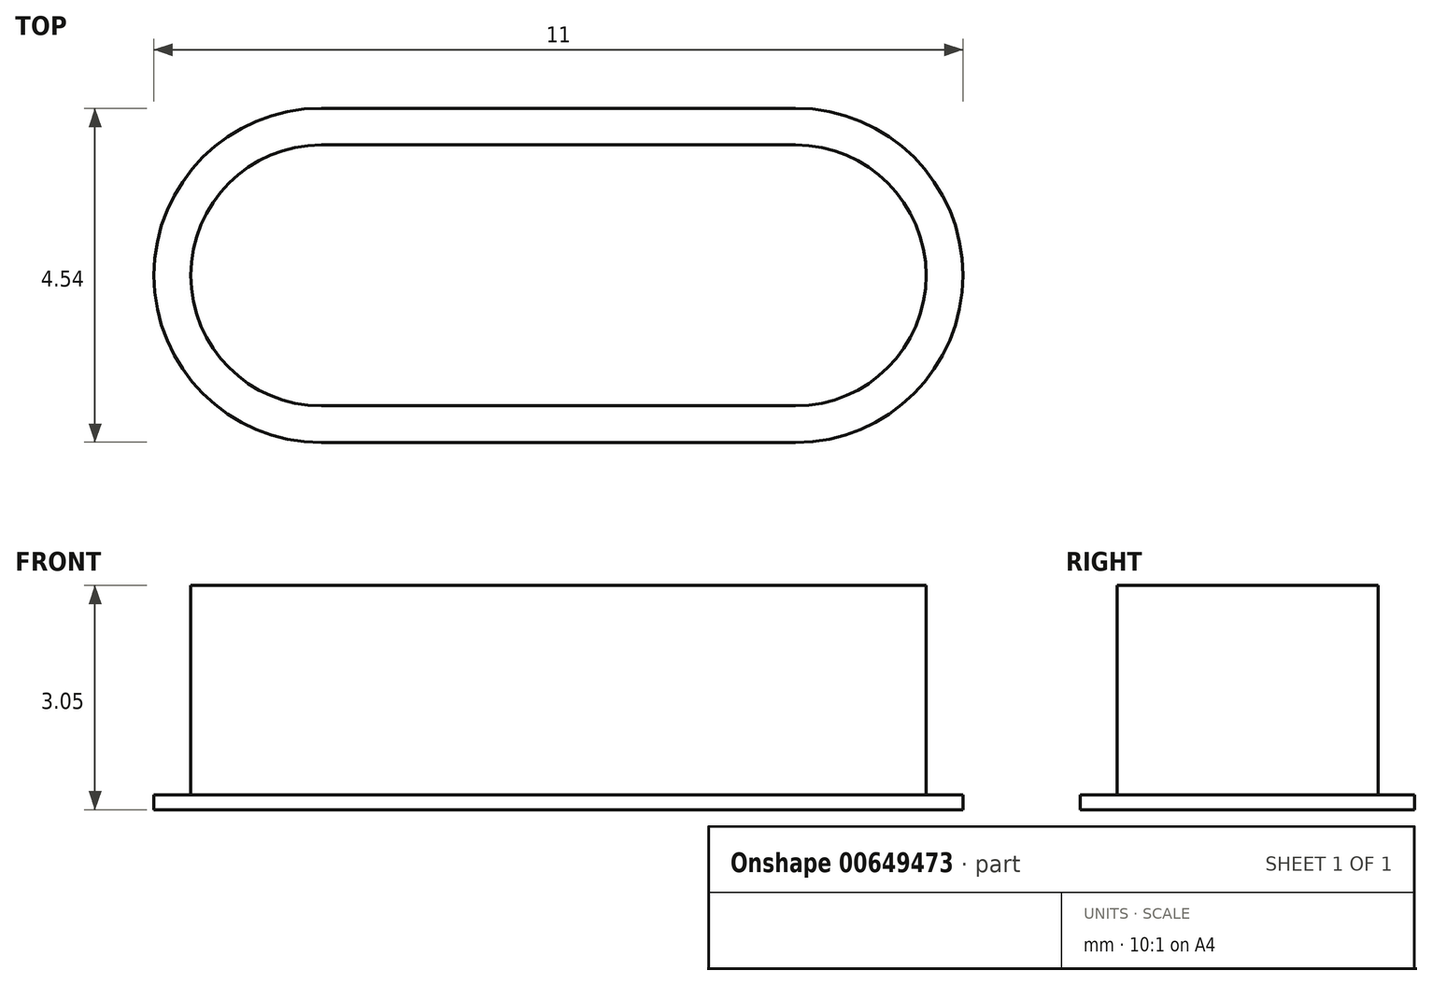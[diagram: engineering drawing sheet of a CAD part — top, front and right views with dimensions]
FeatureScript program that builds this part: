
annotation { "Feature Type Name" : "Feature", "Feature Type Description" : "" }
export const myFeature = defineFeature(function(context is Context, id is Id, definition is map)
    precondition{}
    {
        {
            var Q0;
            Q0=qCreatedBy(makeId("Top.planeOp"),FACE);
            var sketch = newSketch(context, id + "F0", { "sketchPlane" : qUnion([Q0])});
            skLineSegment(sketch, "E0.bottom", {"start": v(3.22, -1.77) * mm, "end": v(-3.22, -1.78) * mm});
            skLineSegment(sketch, "E0.top", {"start": v(3.22, 1.78) * mm, "end": v(-3.22, 1.77) * mm});
            skLineSegment(sketch, "E0.left", {"start": v(3.22, -1.77) * mm, "end": v(3.22, 1.77) * mm, "construction": true});
            skLineSegment(sketch, "E0.right", {"start": v(-3.22, -1.77) * mm, "end": v(-3.23, 1.77) * mm, "construction": true});
            skPoint(sketch, "E0.middle", {"position": v(0, 0) * mm});
            skArc(sketch, "E1", {"start": v(3.22, -1.77) * mm, "mid": v(5, 0) * mm, "end": v(3.22, 1.77) * mm});
            skArc(sketch, "E2", {"start": v(-3.23, 1.78) * mm, "mid": v(-5, 0) * mm, "end": v(-3.22, -1.78) * mm});
            skPoint(sketch, "E3", {"position": v(-5, 0) * mm});
            skPoint(sketch, "E4", {"position": v(5, 0) * mm});
            skSolve(sketch);
        }
        {
            var Q0;
            Q0 = qSketchRegion(id + "F0", true);
            extrude(context, id + "F1", {"entities" : qUnion([Q0]), "depth" : 2.85 * mm, "offsetDistance" : 25 * mm});
        }
        {
            var Q0;
            Q0=makeQuery(id+"F1.opExtrude","CAP_FACE",FACE,{"disambiguationData":[OSD([sQuery(id+"F0.wireOp",EDGE,"E0.bottom"),sQuery(id+"F0.wireOp",EDGE,"E0.top"),sQuery(id+"F0.wireOp",EDGE,"E1"),sQuery(id+"F0.wireOp",EDGE,"E2")])],"isStart":true});
            var sketch = newSketch(context, id + "F2", { "sketchPlane" : qUnion([Q0])});
            skArc(sketch, "E5.0", {"start": v(3.22, -2.27) * mm, "mid": v(5.5, 0) * mm, "end": v(3.22, 2.27) * mm});
            skLineSegment(sketch, "E5.1", {"start": v(-3.23, -2.27) * mm, "end": v(3.22, -2.28) * mm});
            skArc(sketch, "E5.2", {"start": v(-3.22, 2.28) * mm, "mid": v(-5.5, 0) * mm, "end": v(-3.23, -2.28) * mm});
            skLineSegment(sketch, "E5.3", {"start": v(3.22, 2.28) * mm, "end": v(-3.22, 2.28) * mm});
            skSolve(sketch);
        }
        {
            var Q0;
            Q0 = qSketchRegion(id + "F2", true);
            extrude(context, id + "F3", {"entities" : qUnion([Q0]), "operationType" : NewBodyOperationType.ADD, "depth" : .2 * mm, "offsetDistance" : 25 * mm});
        }
        {
            var Q0;
            Q0=makeQuery(id+"F1.opExtrude","SWEPT_EDGE",EDGE,{"disambiguationData":[OSD([sQuery(id+"F0.wireOp",EDGE,"E0.bottom"),sQuery(id+"F0.wireOp",EDGE,"E2")])]});
            var Q1;
            Q1=makeQuery(id+"F1.opExtrude","SWEPT_EDGE",EDGE,{"disambiguationData":[OSD([sQuery(id+"F0.wireOp",EDGE,"E0.top"),sQuery(id+"F0.wireOp",EDGE,"E2")])]});
            cPlane(context, id + "F4", {"entities" : qUnion([Q0, Q1]), "cplaneType" : CPlaneType.LINE_ANGLE, "offset" : 25 * mm, "angle" : 0 * degree, "width" : 150 * mm, "height" : 150 * mm});
        }
        {
            var Q0;
            Q0=makeQuery(id+"F1.opExtrude","CAP_FACE",FACE,{"disambiguationData":[OSD([sQuery(id+"F0.wireOp",EDGE,"E0.bottom"),sQuery(id+"F0.wireOp",EDGE,"E0.top"),sQuery(id+"F0.wireOp",EDGE,"E1"),sQuery(id+"F0.wireOp",EDGE,"E2")])],"isStart":false});
            var sketch = newSketch(context, id + "F5", { "sketchPlane" : qUnion([Q0])});
            skLineSegment(sketch, "E6", {"start": v(-3.22, 1.78) * mm, "end": v(-3.22, -1.78) * mm, "construction": true});
            skLineSegment(sketch, "E7", {"start": v(-3.22, 0) * mm, "end": v(-5, 0) * mm, "construction": true});
            skSolve(sketch);
        }
    });
